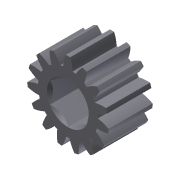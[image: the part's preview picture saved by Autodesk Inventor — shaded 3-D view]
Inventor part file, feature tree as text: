
AUTODESK INVENTOR PART (.ipt)
format: ipt  version: 2011 (Build 150239000, 239)  size: 232,960 bytes
history: native  units: mm (DEFAULTED — no unit token found)
features: other x4, plane x4, sketch x4, extrude x2, revolve x1, mirror x1
ambient origin geometry x8: Origin, YZ Plane, XZ Plane, XY Plane, X Axis, Y Axis, Z Axis, Center Point
bodies: Solid1 (feature_tree)
feature tree (16):
  other  "Gear 15T 20dp 375hex"
  extrude  "Extrusion1"  Depth=11.684mm TaperAngle=0.0deg
  plane  "Work Plane1"
  plane  "Work Plane2"
  plane  "Work Plane3"
  other  "Spur Gear"
  extrude  "Extrusion2"  Depth=76.2mm TaperAngle=0.0deg
  sketch  "Sketch4"  dims[d14=0.0mm d15=47.625mm d16=0.0mm d17=0.0mm d18=0.0mm d19=47.625mm d20=9.525mm d21=25.4mm d22=0.0mm d23=0.79375mm d24=45.0deg d25=90.0deg]
  plane  "Work Plane4"
  revolve  "Revolution1"  [1 undecoded]
  mirror  "Mirror1"
  sketch  "Sketch1"  dims[d0=21.59mm d1=11.684mm d2=0.0mm]
  sketch  "Sketch2"  dims[d3=19.05mm d4=76.2mm d5=0.0mm]
  other  "Srf1"
  sketch  "Sketch3"  dims[d6=0.0mm d7=2.094395mm d9=0.0mm]
  other  "Pitch Diameter"
note: 1 required parameter value undecoded (feature->parameter linkage not recoverable at this tier; creation-order binding heuristic only, values carry confidence <= 0.55)
